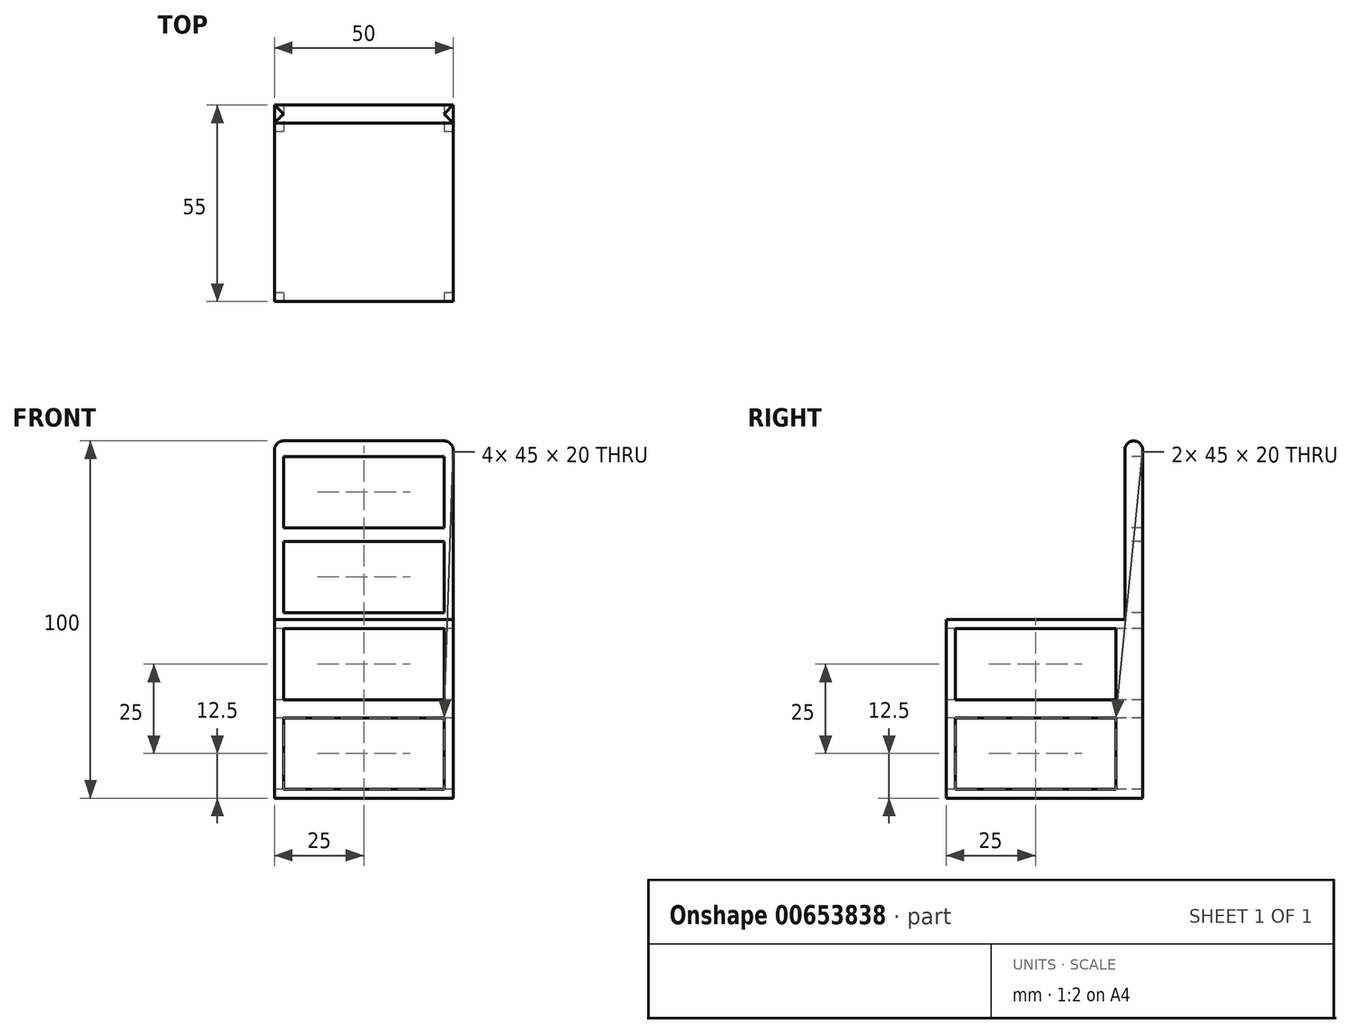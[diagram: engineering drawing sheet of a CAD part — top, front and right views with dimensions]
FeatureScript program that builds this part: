
annotation { "Feature Type Name" : "Feature", "Feature Type Description" : "" }
export const myFeature = defineFeature(function(context is Context, id is Id, definition is map)
    precondition{}
    {
        {
            var Q0;
            Q0=qCreatedBy(makeId("Top.planeOp"),FACE);
            var sketch = newSketch(context, id + "F0", { "sketchPlane" : qUnion([Q0])});
            skLineSegment(sketch, "E0.bottom", {"start": v(25, -25) * mm, "end": v(-25, -25) * mm});
            skLineSegment(sketch, "E0.top", {"start": v(25, 25) * mm, "end": v(-25, 25) * mm});
            skLineSegment(sketch, "E0.left", {"start": v(25, -25) * mm, "end": v(25, 25) * mm});
            skLineSegment(sketch, "E0.right", {"start": v(-25, -25) * mm, "end": v(-25, 25) * mm});
            skPoint(sketch, "E0.middle", {"position": v(0, 0) * mm});
            skLineSegment(sketch, "E1.top", {"start": v(25, 30) * mm, "end": v(-25, 30) * mm});
            skLineSegment(sketch, "E1.left", {"start": v(25, 25) * mm, "end": v(25, 30) * mm});
            skLineSegment(sketch, "E1.right", {"start": v(-25, 25) * mm, "end": v(-25, 30) * mm});
            skSolve(sketch);
        }
        {
            var Q0;
            Q0=makeQuery(id+"F0.imprint","IMPRINT",FACE,{"disambiguationData":[TD([[makeQuery(id+"F0.imprint","IMPRINT",EDGE,{"derivedFrom":sQuery(id+"F0.wireOp",EDGE,"E0.top")}),-1.0]])]});
            extrude(context, id + "F1", {"entities" : qUnion([Q0]), "depth" : 100 * mm, "offsetDistance" : 25 * mm});
        }
        {
            var Q0;
            Q0=makeQuery(id+"F0.imprint","IMPRINT",FACE,{"disambiguationData":[TD([[makeQuery(id+"F0.imprint","IMPRINT",EDGE,{"derivedFrom":sQuery(id+"F0.wireOp",EDGE,"E0.bottom")}),-1.0]])]});
            extrude(context, id + "F2", {"entities" : qUnion([Q0]), "operationType" : NewBodyOperationType.ADD, "depth" : 50 * mm, "offsetDistance" : 25 * mm});
        }
        {
            var Q0;
            Q0=makeQuery(id+"F2.opExtrude","SWEPT_FACE",FACE,{"disambiguationData":[OSD([sQuery(id+"F0.wireOp",EDGE,"E0.bottom")])]});
            var sketch = newSketch(context, id + "F3", { "sketchPlane" : qUnion([Q0])});
            skLineSegment(sketch, "E2", {"start": v(0, 50) * mm, "end": v(0, 0) * mm});
            skPoint(sketch, "E3", {"position": v(0, 25) * mm});
            skLineSegment(sketch, "E4", {"start": v(0, 25) * mm, "end": v(0, 50) * mm});
            skLineSegment(sketch, "E5", {"start": v(0, 25) * mm, "end": v(0, 0) * mm});
            skPoint(sketch, "E6", {"position": v(0, 37.5) * mm});
            skPoint(sketch, "E7", {"position": v(0, 12.5) * mm});
            skLineSegment(sketch, "E8.bottom", {"start": v(22.5, 2.5) * mm, "end": v(-22.5, 2.5) * mm});
            skLineSegment(sketch, "E8.top", {"start": v(22.5, 22.5) * mm, "end": v(-22.5, 22.5) * mm});
            skLineSegment(sketch, "E8.left", {"start": v(22.5, 2.5) * mm, "end": v(22.5, 22.5) * mm});
            skLineSegment(sketch, "E8.right", {"start": v(-22.5, 2.5) * mm, "end": v(-22.5, 22.5) * mm});
            skLineSegment(sketch, "E9.bottom", {"start": v(22.5, 27.5) * mm, "end": v(-22.5, 27.5) * mm});
            skLineSegment(sketch, "E9.top", {"start": v(22.5, 47.5) * mm, "end": v(-22.5, 47.5) * mm});
            skLineSegment(sketch, "E9.left", {"start": v(22.5, 27.5) * mm, "end": v(22.5, 47.5) * mm});
            skLineSegment(sketch, "E9.right", {"start": v(-22.5, 27.5) * mm, "end": v(-22.5, 47.5) * mm});
            skSolve(sketch);
        }
        {
            var Q0;
            {var subQ5=sQuery(id+"F3.wireOp",EDGE,"E9.right");Q0=makeQuery(id+"F3.imprint","IMPRINT",FACE,{"disambiguationData":[TD([[makeQuery(id+"F3.imprint","IMPRINT",EDGE,{"derivedFrom":subQ5}),-1.0]])]});}
            var Q1;
            {var subQ5=sQuery(id+"F3.wireOp",EDGE,"E9.left");Q1=makeQuery(id+"F3.imprint","IMPRINT",FACE,{"disambiguationData":[TD([[makeQuery(id+"F3.imprint","IMPRINT",EDGE,{"derivedFrom":subQ5}),1.0]])]});}
            var Q2;
            {var subQ5=sQuery(id+"F3.wireOp",EDGE,"E8.right");Q2=makeQuery(id+"F3.imprint","IMPRINT",FACE,{"disambiguationData":[TD([[makeQuery(id+"F3.imprint","IMPRINT",EDGE,{"derivedFrom":subQ5}),-1.0]])]});}
            var Q3;
            {var subQ5=sQuery(id+"F3.wireOp",EDGE,"E8.left");Q3=makeQuery(id+"F3.imprint","IMPRINT",FACE,{"disambiguationData":[TD([[makeQuery(id+"F3.imprint","IMPRINT",EDGE,{"derivedFrom":subQ5}),1.0]])]});}
            extrude(context, id + "F4", {"entities" : qUnion([Q0, Q1, Q2, Q3]), "operationType" : NewBodyOperationType.REMOVE, "oppositeDirection" : true, "depth" : 100 * mm, "offsetDistance" : 25 * mm});
        }
        {
            var Q0;
            Q0=makeQuery(id+"F2.boolean.opBoolean","MERGE",FACE,{"derivedFrom":[makeQuery(id+"F1.opExtrude","SWEPT_FACE",FACE,{"disambiguationData":[OSD([sQuery(id+"F0.wireOp",EDGE,"E1.right")])]}),makeQuery(id+"F2.opExtrude","SWEPT_FACE",FACE,{"disambiguationData":[OSD([sQuery(id+"F0.wireOp",EDGE,"E0.right")])]})]});
            var sketch = newSketch(context, id + "F5", { "sketchPlane" : qUnion([Q0])});
            skLineSegment(sketch, "E10", {"start": v(-25, 50) * mm, "end": v(-25, 0) * mm});
            skLineSegment(sketch, "E11", {"start": v(0, 0) * mm, "end": v(0, 50) * mm});
            skLineSegment(sketch, "E12", {"start": v(-25, 25) * mm, "end": v(25, 25) * mm});
            skLineSegment(sketch, "E13", {"start": v(0, 25) * mm, "end": v(0, 50) * mm});
            skLineSegment(sketch, "E14", {"start": v(0, 25) * mm, "end": v(0, 0) * mm});
            skPoint(sketch, "E15", {"position": v(0, 37.5) * mm});
            skPoint(sketch, "E16", {"position": v(0, 12.5) * mm});
            skLineSegment(sketch, "E17.bottom", {"start": v(22.5, 27.5) * mm, "end": v(-22.5, 27.5) * mm});
            skLineSegment(sketch, "E17.top", {"start": v(22.5, 47.5) * mm, "end": v(-22.5, 47.5) * mm});
            skLineSegment(sketch, "E17.left", {"start": v(22.5, 27.5) * mm, "end": v(22.5, 47.5) * mm});
            skLineSegment(sketch, "E17.right", {"start": v(-22.5, 27.5) * mm, "end": v(-22.5, 47.5) * mm});
            skLineSegment(sketch, "E18.bottom", {"start": v(22.5, 2.5) * mm, "end": v(-22.5, 2.5) * mm});
            skLineSegment(sketch, "E18.top", {"start": v(22.5, 22.5) * mm, "end": v(-22.5, 22.5) * mm});
            skLineSegment(sketch, "E18.left", {"start": v(22.5, 2.5) * mm, "end": v(22.5, 22.5) * mm});
            skLineSegment(sketch, "E18.right", {"start": v(-22.5, 2.5) * mm, "end": v(-22.5, 22.5) * mm});
            skSolve(sketch);
        }
        {
            var Q0;
            {var subQ5=sQuery(id+"F5.wireOp",EDGE,"E17.right");Q0=makeQuery(id+"F5.imprint","IMPRINT",FACE,{"disambiguationData":[TD([[makeQuery(id+"F5.imprint","IMPRINT",EDGE,{"derivedFrom":subQ5}),-1.0]])]});}
            var Q1;
            {var subQ5=sQuery(id+"F5.wireOp",EDGE,"E17.left");Q1=makeQuery(id+"F5.imprint","IMPRINT",FACE,{"disambiguationData":[TD([[makeQuery(id+"F5.imprint","IMPRINT",EDGE,{"derivedFrom":subQ5}),1.0]])]});}
            var Q2;
            {var subQ5=sQuery(id+"F5.wireOp",EDGE,"E18.left");Q2=makeQuery(id+"F5.imprint","IMPRINT",FACE,{"disambiguationData":[TD([[makeQuery(id+"F5.imprint","IMPRINT",EDGE,{"derivedFrom":subQ5}),1.0]])]});}
            var Q3;
            {var subQ5=sQuery(id+"F5.wireOp",EDGE,"E18.right");Q3=makeQuery(id+"F5.imprint","IMPRINT",FACE,{"disambiguationData":[TD([[makeQuery(id+"F5.imprint","IMPRINT",EDGE,{"derivedFrom":subQ5}),-1.0]])]});}
            extrude(context, id + "F6", {"entities" : qUnion([Q0, Q1, Q2, Q3]), "operationType" : NewBodyOperationType.REMOVE, "oppositeDirection" : true, "depth" : 55 * mm, "offsetDistance" : 25 * mm});
        }
        {
            var Q0;
            Q0=makeQuery(id+"F1.opExtrude","CAP_EDGE",EDGE,{"disambiguationData":[OSD([sQuery(id+"F0.wireOp",EDGE,"E0.top")])],"isStart":false});
            var Q1;
            Q1=makeQuery(id+"F1.opExtrude","CAP_FACE",FACE,{"disambiguationData":[OSD([sQuery(id+"F0.wireOp",EDGE,"E0.top"),sQuery(id+"F0.wireOp",EDGE,"E1.top"),sQuery(id+"F0.wireOp",EDGE,"E1.left"),sQuery(id+"F0.wireOp",EDGE,"E1.right")])],"isStart":false});
            fillet(context, id + "F7", {"entities" : qUnion([Q0, Q1]), "radius" : 2.5 * mm, "tangentPropagation" : true, "allowEdgeOverflow" : false});
        }
        {
            var Q0;
            Q0=makeQuery(id+"F1.opExtrude","SWEPT_FACE",FACE,{"disambiguationData":[OSD([sQuery(id+"F0.wireOp",EDGE,"E0.top")])]});
            var sketch = newSketch(context, id + "F8", { "sketchPlane" : qUnion([Q0])});
            skLineSegment(sketch, "E19", {"start": v(0, 50) * mm, "end": v(0, 97.5) * mm, "construction": true});
            skPoint(sketch, "E20", {"position": v(0, 73.75) * mm});
            skLineSegment(sketch, "E21", {"start": v(0, 97.5) * mm, "end": v(0, 73.75) * mm, "construction": true});
            skLineSegment(sketch, "E22", {"start": v(0, 50) * mm, "end": v(0, 73.75) * mm, "construction": true});
            skPoint(sketch, "E23", {"position": v(0, 61.88) * mm});
            skLineSegment(sketch, "E24.bottom", {"start": v(22.5, 75.62) * mm, "end": v(-22.5, 75.62) * mm});
            skLineSegment(sketch, "E24.top", {"start": v(22.5, 95.62) * mm, "end": v(-22.5, 95.62) * mm});
            skLineSegment(sketch, "E24.left", {"start": v(22.5, 75.62) * mm, "end": v(22.5, 95.62) * mm});
            skLineSegment(sketch, "E24.right", {"start": v(-22.5, 75.62) * mm, "end": v(-22.5, 95.62) * mm});
            skPoint(sketch, "E24.middle", {"position": v(0, 85.62) * mm});
            skLineSegment(sketch, "E25.bottom", {"start": v(22.5, 51.88) * mm, "end": v(-22.5, 51.88) * mm});
            skLineSegment(sketch, "E25.top", {"start": v(22.5, 71.88) * mm, "end": v(-22.5, 71.88) * mm});
            skLineSegment(sketch, "E25.left", {"start": v(22.5, 51.88) * mm, "end": v(22.5, 71.88) * mm});
            skLineSegment(sketch, "E25.right", {"start": v(-22.5, 51.88) * mm, "end": v(-22.5, 71.88) * mm});
            skSolve(sketch);
        }
        {
            var Q0;
            Q0=makeQuery(id+"F8.imprint","IMPRINT",FACE,{"disambiguationData":[TD([[makeQuery(id+"F8.imprint","IMPRINT",EDGE,{"derivedFrom":sQuery(id+"F8.wireOp",EDGE,"E24.bottom")}),-1.0]])]});
            var Q1;
            Q1=makeQuery(id+"F8.imprint","IMPRINT",FACE,{"disambiguationData":[TD([[makeQuery(id+"F8.imprint","IMPRINT",EDGE,{"derivedFrom":sQuery(id+"F8.wireOp",EDGE,"E25.bottom")}),-1.0]])]});
            extrude(context, id + "F9", {"entities" : qUnion([Q0, Q1]), "operationType" : NewBodyOperationType.REMOVE, "oppositeDirection" : true, "depth" : 25 * mm, "offsetDistance" : 25 * mm});
        }
    });
